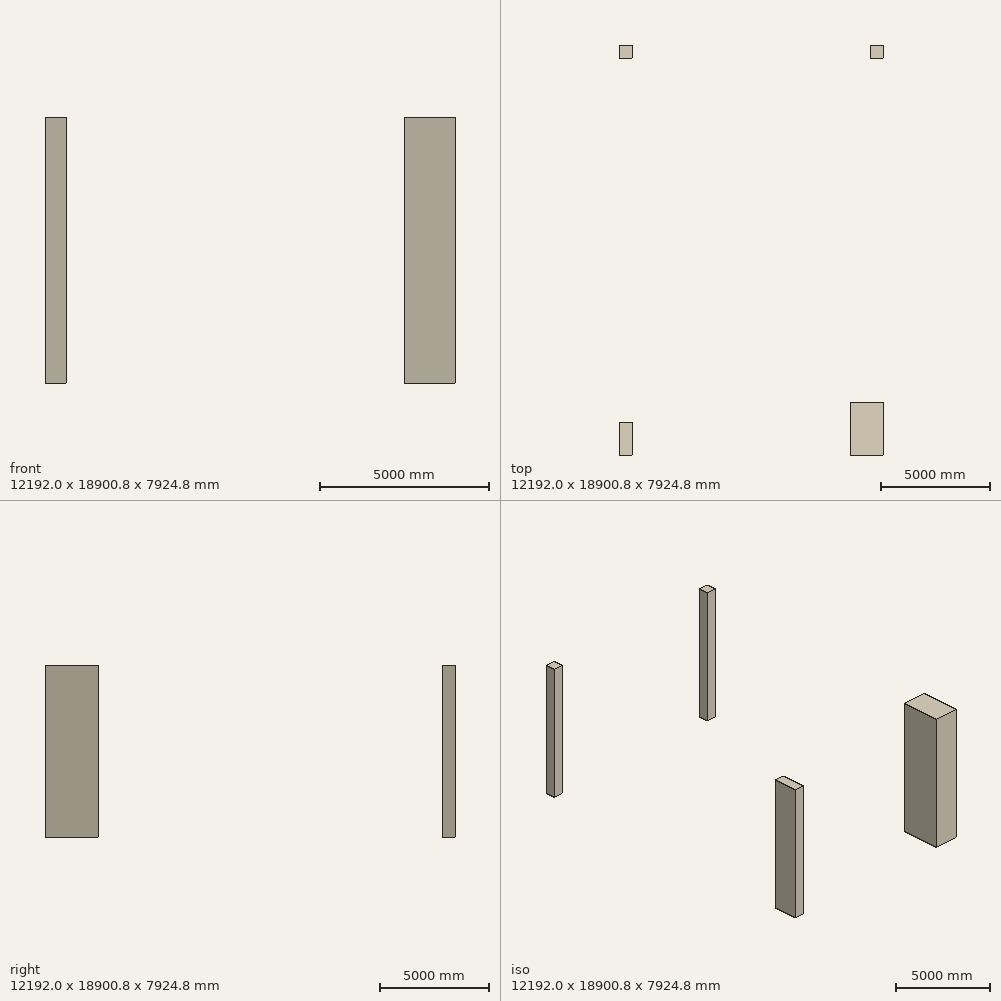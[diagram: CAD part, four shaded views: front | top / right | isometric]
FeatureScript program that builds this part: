
annotation { "Feature Type Name" : "Feature", "Feature Type Description" : "" }
export const myFeature = defineFeature(function(context is Context, id is Id, definition is map)
    precondition{}
    {
        {
            var Q0;
            Q0=qCreatedBy(makeId("Top.planeOp"),FACE);
            var sketch = newSketch(context, id + "F0", { "sketchPlane" : qUnion([Q0])});
            skLineSegment(sketch, "E0.bottom", {"start": v(-5486.4, 8382) * mm, "end": v(5486.4, 8382) * mm});
            skLineSegment(sketch, "E0.top", {"start": v(-5486.4, -8382) * mm, "end": v(5486.4, -8382) * mm});
            skLineSegment(sketch, "E0.left", {"start": v(-5486.4, 8382) * mm, "end": v(-5486.4, -8382) * mm});
            skLineSegment(sketch, "E0.right", {"start": v(5486.4, 8382) * mm, "end": v(5486.4, -8382) * mm});
            skPoint(sketch, "E0.middle", {"position": v(0, 0) * mm});
            skSolve(sketch);
        }
        {
            var Q0;
            Q0=makeQuery(id+"F0.imprint","IMPRINT",FACE,{"disambiguationData":[TD([[makeQuery(id+"F0.imprint","IMPRINT",EDGE,{"derivedFrom":sQuery(id+"F0.wireOp",EDGE,"E0.bottom")}),-1.0]])]});
            var sketch = newSketch(context, id + "F1", { "sketchPlane" : qUnion([Q0])});
            skLineSegment(sketch, "E1.bottom", {"start": v(4572, -7470.76) * mm, "end": v(5486.4, -7470.76) * mm});
            skLineSegment(sketch, "E1.left", {"start": v(4572, -7470.76) * mm, "end": v(4572, -8385.16) * mm});
            skPoint(sketch, "E2", {"position": v(5486.4, -8382) * mm});
            skSolve(sketch);
        }
        {
            var Q0;
            {var subQ3=sQuery(id+"F1.wireOp",EDGE,"E1.bottom");Q0=makeQuery(id+"F1.imprint","IMPRINT",FACE,{"disambiguationData":[TD([[makeQuery(id+"F1.imprint","IMPRINT",EDGE,{"derivedFrom":subQ3}),1.0]])]});}
            var sketch = newSketch(context, id + "F2", { "sketchPlane" : qUnion([Q0])});
            skPoint(sketch, "E3", {"position": v(-5486.4, -5029.2) * mm});
            skSolve(sketch);
        }
        {
            var Q0;
            {var subQ3=sQuery(id+"F1.wireOp",EDGE,"E1.bottom");Q0=makeQuery(id+"F1.imprint","IMPRINT",FACE,{"disambiguationData":[TD([[makeQuery(id+"F1.imprint","IMPRINT",EDGE,{"derivedFrom":subQ3}),1.0]])]});}
            var sketch = newSketch(context, id + "F3", { "sketchPlane" : qUnion([Q0])});
            skPoint(sketch, "E4", {"position": v(-5486.4, -1676.4) * mm});
            skSolve(sketch);
        }
        {
            var Q0;
            {var subQ3=sQuery(id+"F1.wireOp",EDGE,"E1.bottom");Q0=makeQuery(id+"F1.imprint","IMPRINT",FACE,{"disambiguationData":[TD([[makeQuery(id+"F1.imprint","IMPRINT",EDGE,{"derivedFrom":subQ3}),1.0]])]});}
            var sketch = newSketch(context, id + "F4", { "sketchPlane" : qUnion([Q0])});
            skPoint(sketch, "E5", {"position": v(-5486.4, 1676.4) * mm});
            skSolve(sketch);
        }
        {
            var Q0;
            {var subQ3=sQuery(id+"F1.wireOp",EDGE,"E1.bottom");Q0=makeQuery(id+"F1.imprint","IMPRINT",FACE,{"disambiguationData":[TD([[makeQuery(id+"F1.imprint","IMPRINT",EDGE,{"derivedFrom":subQ3}),1.0]])]});}
            var sketch = newSketch(context, id + "F5", { "sketchPlane" : qUnion([Q0])});
            skPoint(sketch, "E6", {"position": v(-5486.4, 5029.2) * mm});
            skSolve(sketch);
        }
        {
            var Q0;
            {var subQ3=sQuery(id+"F1.wireOp",EDGE,"E1.bottom");Q0=makeQuery(id+"F1.imprint","IMPRINT",FACE,{"disambiguationData":[TD([[makeQuery(id+"F1.imprint","IMPRINT",EDGE,{"derivedFrom":subQ3}),1.0]])]});}
            var sketch = newSketch(context, id + "F6", { "sketchPlane" : qUnion([Q0])});
            skPoint(sketch, "E7", {"position": v(-2743.2, 8382) * mm});
            skSolve(sketch);
        }
        {
            var Q0;
            {var subQ3=sQuery(id+"F1.wireOp",EDGE,"E1.bottom");Q0=makeQuery(id+"F1.imprint","IMPRINT",FACE,{"disambiguationData":[TD([[makeQuery(id+"F1.imprint","IMPRINT",EDGE,{"derivedFrom":subQ3}),1.0]])]});}
            var sketch = newSketch(context, id + "F7", { "sketchPlane" : qUnion([Q0])});
            skPoint(sketch, "E8", {"position": v(0, 8382) * mm});
            skSolve(sketch);
        }
        {
            var Q0;
            {var subQ3=sQuery(id+"F1.wireOp",EDGE,"E1.bottom");Q0=makeQuery(id+"F1.imprint","IMPRINT",FACE,{"disambiguationData":[TD([[makeQuery(id+"F1.imprint","IMPRINT",EDGE,{"derivedFrom":subQ3}),1.0]])]});}
            var sketch = newSketch(context, id + "F8", { "sketchPlane" : qUnion([Q0])});
            skPoint(sketch, "E9", {"position": v(5486.4, 5029.2) * mm});
            skPoint(sketch, "E10", {"position": v(5486.4, 1676.4) * mm});
            skPoint(sketch, "E11", {"position": v(5486.4, -1676.4) * mm});
            skPoint(sketch, "E12", {"position": v(5486.4, -5029.2) * mm});
            skSolve(sketch);
        }
        {
            var Q0;
            {var subQ3=sQuery(id+"F1.wireOp",EDGE,"E1.bottom");Q0=makeQuery(id+"F1.imprint","IMPRINT",FACE,{"disambiguationData":[TD([[makeQuery(id+"F1.imprint","IMPRINT",EDGE,{"derivedFrom":subQ3}),1.0]])]});}
            var sketch = newSketch(context, id + "F9", { "sketchPlane" : qUnion([Q0])});
            skPoint(sketch, "E13", {"position": v(2743.2, -8382) * mm});
            skPoint(sketch, "E14", {"position": v(0, -8382) * mm});
            skPoint(sketch, "E15", {"position": v(-2743.2, -8382) * mm});
            skSolve(sketch);
        }
        {
            var Q0;
            {var subQ3=sQuery(id+"F1.wireOp",EDGE,"E1.bottom");Q0=makeQuery(id+"F1.imprint","IMPRINT",FACE,{"disambiguationData":[TD([[makeQuery(id+"F1.imprint","IMPRINT",EDGE,{"derivedFrom":subQ3}),1.0]])]});}
            var sketch = newSketch(context, id + "F10", { "sketchPlane" : qUnion([Q0])});
            skPoint(sketch, "E16", {"position": v(0, 5029.2) * mm});
            skPoint(sketch, "E17", {"position": v(0, 1676.4) * mm});
            skPoint(sketch, "E18", {"position": v(0, -1676.4) * mm});
            skPoint(sketch, "E19", {"position": v(0, -5029.2) * mm});
            skLineSegment(sketch, "E20.bottom", {"start": v(5486.4, -8382) * mm, "end": v(-5486.4, -8382) * mm});
            skLineSegment(sketch, "E20.top", {"start": v(5486.4, 8382) * mm, "end": v(-5486.4, 8382) * mm});
            skLineSegment(sketch, "E20.left", {"start": v(5486.4, -8382) * mm, "end": v(5486.4, 8382) * mm});
            skLineSegment(sketch, "E20.right", {"start": v(-5486.4, -8382) * mm, "end": v(-5486.4, 8382) * mm});
            skPoint(sketch, "E20.middle", {"position": v(0, 0) * mm});
            skSolve(sketch);
        }
        {
            var Q0;
            Q0=qCreatedBy(makeId("Top.planeOp"),FACE);
            var sketch = newSketch(context, id + "F11", { "sketchPlane" : qUnion([Q0])});
            skLineSegment(sketch, "E21.bottom", {"start": v(5486.4, 8382) * mm, "end": v(6096, 8382) * mm});
            skLineSegment(sketch, "E21.top", {"start": v(5486.4, 8991.6) * mm, "end": v(6096, 8991.6) * mm});
            skLineSegment(sketch, "E21.left", {"start": v(5486.4, 8382) * mm, "end": v(5486.4, 8991.6) * mm});
            skLineSegment(sketch, "E21.right", {"start": v(6096, 8382) * mm, "end": v(6096, 8991.6) * mm});
            skSolve(sketch);
        }
        {
            var Q0;
            Q0=qCreatedBy(makeId("Top.planeOp"),FACE);
            var sketch = newSketch(context, id + "F12", { "sketchPlane" : qUnion([Q0])});
            skLineSegment(sketch, "E22.bottom", {"start": v(-5486.4, 8382) * mm, "end": v(-6096, 8382) * mm});
            skLineSegment(sketch, "E22.top", {"start": v(-5486.4, 8991.6) * mm, "end": v(-6096, 8991.6) * mm});
            skLineSegment(sketch, "E22.left", {"start": v(-5486.4, 8382) * mm, "end": v(-5486.4, 8991.6) * mm});
            skLineSegment(sketch, "E22.right", {"start": v(-6096, 8382) * mm, "end": v(-6096, 8991.6) * mm});
            skLineSegment(sketch, "E23.bottom", {"start": v(-5486.4, -8382) * mm, "end": v(-6096, -8382) * mm});
            skLineSegment(sketch, "E23.top", {"start": v(-5486.4, -9906) * mm, "end": v(-6096, -9906) * mm});
            skLineSegment(sketch, "E23.left", {"start": v(-5486.4, -8382) * mm, "end": v(-5486.4, -9906) * mm});
            skLineSegment(sketch, "E23.right", {"start": v(-6096, -8382) * mm, "end": v(-6096, -9906) * mm});
            skLineSegment(sketch, "E24.bottom", {"start": v(4572, -7470.76) * mm, "end": v(6096, -7470.76) * mm});
            skLineSegment(sketch, "E24.top", {"start": v(4572, -9909.16) * mm, "end": v(6096, -9909.16) * mm});
            skLineSegment(sketch, "E24.left", {"start": v(4572, -7470.76) * mm, "end": v(4572, -9909.16) * mm});
            skLineSegment(sketch, "E24.right", {"start": v(6096, -7470.76) * mm, "end": v(6096, -9909.16) * mm});
            skSolve(sketch);
        }
        {
            var Q0;
            Q0 = qSketchRegion(id + "F12", true);
            extrude(context, id + "F13", {"entities" : qUnion([Q0]), "depth" : 1828.8 * mm, "offsetDistance" : 30.48 * mm, "hasSecondDirection" : true, "secondDirectionOppositeDirection" : true, "secondDirectionDepth" : 6096 * mm});
        }
        {
            var Q0;
            Q0=makeQuery(id+"F11.imprint","IMPRINT",FACE,{"disambiguationData":[TD([[makeQuery(id+"F11.imprint","IMPRINT",EDGE,{"derivedFrom":sQuery(id+"F11.wireOp",EDGE,"E21.bottom")}),1.0]])]});
            extrude(context, id + "F14", {"entities" : qUnion([Q0]), "oppositeDirection" : true, "depth" : 6096 * mm, "offsetDistance" : 30.48 * mm, "hasSecondDirection" : true, "secondDirectionOppositeDirection" : false, "secondDirectionDepth" : 1828.8 * mm});
        }
        {
            var Q0;
            Q0=makeQuery(id+"F13.opExtrude","CAP_FACE",FACE,{"disambiguationData":[OSD([sQuery(id+"F12.wireOp",EDGE,"E24.bottom"),sQuery(id+"F12.wireOp",EDGE,"E24.top"),sQuery(id+"F12.wireOp",EDGE,"E24.left"),sQuery(id+"F12.wireOp",EDGE,"E24.right")])],"isStart":false});
            var Q1;
            Q1=makeQuery(id+"F13.opExtrude","CAP_VERTEX",VERTEX,{"disambiguationData":[OSD([sQuery(id+"F12.wireOp",EDGE,"E22.bottom"),sQuery(id+"F12.wireOp",EDGE,"E22.left")])],"isStart":false});
            cPlane(context, id + "F15", {"entities" : qUnion([Q0, Q1]), "cplaneType" : CPlaneType.PLANE_POINT, "offset" : 25.4 * mm, "width" : 152.4 * mm, "height" : 152.4 * mm});
        }
        {
            var Q0;
            Q0=qCreatedBy(id+"F15.planeOp",FACE);
            var sketch = newSketch(context, id + "F16", { "sketchPlane" : qUnion([Q0])});
            skLineSegment(sketch, "E25.bottom", {"start": v(6096, -9909.16) * mm, "end": v(-6096, -9909.16) * mm});
            skLineSegment(sketch, "E25.top", {"start": v(6096, 8991.6) * mm, "end": v(-6096, 8991.6) * mm});
            skLineSegment(sketch, "E25.left", {"start": v(6096, -9909.16) * mm, "end": v(6096, 8991.6) * mm});
            skLineSegment(sketch, "E25.right", {"start": v(-6096, -9909.16) * mm, "end": v(-6096, 8991.6) * mm});
            skSolve(sketch);
        }
        {
            var Q0;
            Q0=makeQuery(id+"F13.opExtrude","CAP_VERTEX",VERTEX,{"disambiguationData":[OSD([sQuery(id+"F12.wireOp",EDGE,"E24.bottom"),sQuery(id+"F12.wireOp",EDGE,"E24.left")])],"isStart":true});
            var Q1;
            Q1=qCreatedBy(makeId("Top.planeOp"),FACE);
            cPlane(context, id + "F17", {"entities" : qUnion([Q0, Q1]), "cplaneType" : CPlaneType.PLANE_POINT, "offset" : 25.4 * mm, "width" : 152.4 * mm, "height" : 152.4 * mm});
        }
        {
            var Q0;
            Q0=qCreatedBy(id+"F17.planeOp",FACE);
            var sketch = newSketch(context, id + "F18", { "sketchPlane" : qUnion([Q0])});
            skLineSegment(sketch, "E26.bottom", {"start": v(6096, -9909.16) * mm, "end": v(-6096, -9909.16) * mm});
            skLineSegment(sketch, "E26.top", {"start": v(6096, 8991.6) * mm, "end": v(-6096, 8991.6) * mm});
            skLineSegment(sketch, "E26.left", {"start": v(6096, -9909.16) * mm, "end": v(6096, 8991.6) * mm});
            skLineSegment(sketch, "E26.right", {"start": v(-6096, -9909.16) * mm, "end": v(-6096, 8991.6) * mm});
            skSolve(sketch);
        }
        {
            var Q0;
            Q0=makeQuery(id+"F13.opExtrude","CAP_VERTEX",VERTEX,{"disambiguationData":[OSD([sQuery(id+"F12.wireOp",EDGE,"E22.top"),sQuery(id+"F12.wireOp",EDGE,"E22.left")])],"isStart":true});
            var Q1;
            Q1=qCreatedBy(makeId("Front.planeOp"),FACE);
            cPlane(context, id + "F19", {"entities" : qUnion([Q0, Q1]), "cplaneType" : CPlaneType.PLANE_POINT, "offset" : 25.4 * mm, "width" : 152.4 * mm, "height" : 152.4 * mm});
        }
        {
            var Q0;
            Q0=qCreatedBy(id+"F19.planeOp",FACE);
            var sketch = newSketch(context, id + "F20", { "sketchPlane" : qUnion([Q0])});
            skLineSegment(sketch, "E27.bottom", {"start": v(6096, -6096) * mm, "end": v(-6096, -6096) * mm});
            skLineSegment(sketch, "E27.top", {"start": v(6096, 1828.8) * mm, "end": v(-6096, 1828.8) * mm});
            skLineSegment(sketch, "E27.left", {"start": v(6096, -6096) * mm, "end": v(6096, 1828.8) * mm});
            skLineSegment(sketch, "E27.right", {"start": v(-6096, -6096) * mm, "end": v(-6096, 1828.8) * mm});
            skSolve(sketch);
        }
        {
            var Q0;
            Q0=makeQuery(id+"F13.opExtrude","CAP_VERTEX",VERTEX,{"disambiguationData":[OSD([sQuery(id+"F12.wireOp",EDGE,"E24.top"),sQuery(id+"F12.wireOp",EDGE,"E24.left")])],"isStart":true});
            var Q1;
            Q1=qCreatedBy(makeId("Front.planeOp"),FACE);
            cPlane(context, id + "F21", {"entities" : qUnion([Q0, Q1]), "cplaneType" : CPlaneType.PLANE_POINT, "offset" : 25.4 * mm, "width" : 152.4 * mm, "height" : 152.4 * mm});
        }
        {
            var Q0;
            Q0=qCreatedBy(id+"F21.planeOp",FACE);
            var sketch = newSketch(context, id + "F22", { "sketchPlane" : qUnion([Q0])});
            skLineSegment(sketch, "E28.bottom", {"start": v(-6096, 1828.8) * mm, "end": v(6096, 1828.8) * mm});
            skLineSegment(sketch, "E28.top", {"start": v(-6096, -6096) * mm, "end": v(6096, -6096) * mm});
            skLineSegment(sketch, "E28.left", {"start": v(-6096, 1828.8) * mm, "end": v(-6096, -6096) * mm});
            skLineSegment(sketch, "E28.right", {"start": v(6096, 1828.8) * mm, "end": v(6096, -6096) * mm});
            skSolve(sketch);
        }
        {
            var Q0;
            Q0=makeQuery(id+"F13.opExtrude","CAP_VERTEX",VERTEX,{"disambiguationData":[OSD([sQuery(id+"F12.wireOp",EDGE,"E23.bottom"),sQuery(id+"F12.wireOp",EDGE,"E23.right")])],"isStart":true});
            var Q1;
            Q1=qCreatedBy(makeId("Right.planeOp"),FACE);
            cPlane(context, id + "F23", {"entities" : qUnion([Q0, Q1]), "cplaneType" : CPlaneType.PLANE_POINT, "offset" : 25.4 * mm, "width" : 152.4 * mm, "height" : 152.4 * mm});
        }
        {
            var Q0;
            Q0=makeQuery(id+"F14.opExtrude","CAP_VERTEX",VERTEX,{"disambiguationData":[OSD([sQuery(id+"F11.wireOp",EDGE,"E21.bottom"),sQuery(id+"F11.wireOp",EDGE,"E21.right")])],"isStart":false});
            var Q1;
            Q1=qCreatedBy(makeId("Right.planeOp"),FACE);
            cPlane(context, id + "F24", {"entities" : qUnion([Q0, Q1]), "cplaneType" : CPlaneType.PLANE_POINT, "offset" : 25.4 * mm, "width" : 152.4 * mm, "height" : 152.4 * mm});
        }
        {
            var Q0;
            Q0=makeQuery(id+"F13.opExtrude","CAP_VERTEX",VERTEX,{"disambiguationData":[OSD([sQuery(id+"F12.wireOp",EDGE,"E23.bottom"),sQuery(id+"F12.wireOp",EDGE,"E23.left")])],"isStart":true});
            var Q1;
            Q1=qCreatedBy(makeId("Front.planeOp"),FACE);
            cPlane(context, id + "F25", {"entities" : qUnion([Q0, Q1]), "cplaneType" : CPlaneType.PLANE_POINT, "offset" : 25.4 * mm, "width" : 152.4 * mm, "height" : 152.4 * mm});
        }
        {
            var Q0;
            Q0=qCreatedBy(id+"F25.planeOp",FACE);
            var sketch = newSketch(context, id + "F26", { "sketchPlane" : qUnion([Q0])});
            skLineSegment(sketch, "E29.bottom", {"start": v(-5486.4, 0) * mm, "end": v(4572, 0) * mm});
            skLineSegment(sketch, "E29.top", {"start": v(-5486.4, -6096) * mm, "end": v(4572, -6096) * mm});
            skLineSegment(sketch, "E29.left", {"start": v(-5486.4, 0) * mm, "end": v(-5486.4, -6096) * mm});
            skLineSegment(sketch, "E29.right", {"start": v(4572, 0) * mm, "end": v(4572, -6096) * mm});
            skSolve(sketch);
        }
        {
            var Q0;
            Q0=makeQuery(id+"F14.opExtrude","CAP_VERTEX",VERTEX,{"disambiguationData":[OSD([sQuery(id+"F11.wireOp",EDGE,"E21.bottom"),sQuery(id+"F11.wireOp",EDGE,"E21.left")])],"isStart":false});
            var Q1;
            Q1=qCreatedBy(makeId("Front.planeOp"),FACE);
            cPlane(context, id + "F27", {"entities" : qUnion([Q0, Q1]), "cplaneType" : CPlaneType.PLANE_POINT, "offset" : 25.4 * mm, "width" : 152.4 * mm, "height" : 152.4 * mm});
        }
        {
            var Q0;
            Q0=qCreatedBy(id+"F27.planeOp",FACE);
            var sketch = newSketch(context, id + "F28", { "sketchPlane" : qUnion([Q0])});
            skLineSegment(sketch, "E30.bottom", {"start": v(5486.4, -6096) * mm, "end": v(-5486.4, -6096) * mm});
            skLineSegment(sketch, "E30.top", {"start": v(5486.4, 0) * mm, "end": v(-5486.4, 0) * mm});
            skLineSegment(sketch, "E30.left", {"start": v(5486.4, -6096) * mm, "end": v(5486.4, 0) * mm});
            skLineSegment(sketch, "E30.right", {"start": v(-5486.4, -6096) * mm, "end": v(-5486.4, 0) * mm});
            skSolve(sketch);
        }
        {
            var Q0;
            Q0=sQuery(id+"F28.wireOp",VERTEX,"E30.bottom.start");
            var Q1;
            Q1=qCreatedBy(makeId("Right.planeOp"),FACE);
            cPlane(context, id + "F29", {"entities" : qUnion([Q0, Q1]), "cplaneType" : CPlaneType.PLANE_POINT, "offset" : 25.4 * mm, "width" : 152.4 * mm, "height" : 152.4 * mm});
        }
        {
            var Q0;
            Q0=sQuery(id+"F28.wireOp",VERTEX,"E30.bottom.end");
            var Q1;
            Q1=qCreatedBy(makeId("Right.planeOp"),FACE);
            cPlane(context, id + "F30", {"entities" : qUnion([Q0, Q1]), "cplaneType" : CPlaneType.PLANE_POINT, "offset" : 25.4 * mm, "width" : 152.4 * mm, "height" : 152.4 * mm});
        }
        {
            var Q0;
            Q0=makeQuery(id+"F13.opExtrude","CAP_VERTEX",VERTEX,{"disambiguationData":[OSD([sQuery(id+"F12.wireOp",EDGE,"E24.bottom"),sQuery(id+"F12.wireOp",EDGE,"E24.left")])],"isStart":true});
            var Q1;
            Q1=qCreatedBy(makeId("Front.planeOp"),FACE);
            cPlane(context, id + "F31", {"entities" : qUnion([Q0, Q1]), "cplaneType" : CPlaneType.PLANE_POINT, "offset" : 25.4 * mm, "width" : 152.4 * mm, "height" : 152.4 * mm});
        }
        {
            var Q0;
            Q0=makeQuery(id+"F13.opExtrude","CAP_VERTEX",VERTEX,{"disambiguationData":[OSD([sQuery(id+"F12.wireOp",EDGE,"E24.bottom"),sQuery(id+"F12.wireOp",EDGE,"E24.left")])],"isStart":true});
            var Q1;
            Q1=qCreatedBy(makeId("Right.planeOp"),FACE);
            cPlane(context, id + "F32", {"entities" : qUnion([Q0, Q1]), "cplaneType" : CPlaneType.PLANE_POINT, "offset" : 25.4 * mm, "width" : 152.4 * mm, "height" : 152.4 * mm});
        }
    });
